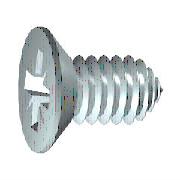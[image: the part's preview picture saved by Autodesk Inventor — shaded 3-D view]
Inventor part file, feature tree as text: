
AUTODESK INVENTOR PART (.ipt)
format: ipt  version: 2020 (Build 240168000, 168)  size: 263,680 bytes
history: native  units: mm (DEFAULTED — no unit token found)
features: extrude x2, plane x1, sketch x1
ambient origin geometry x8: Origin, YZ Plane, XZ Plane, XY Plane, X Axis, Y Axis, Z Axis, Center Point
bodies: Solid1 (feature_tree), Body (feature_tree)
feature tree (4):
  extrude  "Slot"  TaperAngle=45.0deg  [1 undecoded]
  extrude  "Star Cut"  Depth=2.2mm
  plane  "Work Plane2"
  sketch  "Sketch3"  dims[d0=32.0mm d2=45.0deg d3=4.2mm d5=8.4mm d6=4.4mm d7=4.625123mm d8=10.821041mm d9=2.51mm d16=90.0deg d10=45.0deg d11=1.76mm d12=4.4mm d13=0.515mm d14=4.4mm d15=45.0deg d17=0.515mm d18=2.6mm d19=-5.235988mm d20=29.4mm d21=0.0mm d22=2.1mm d23=3.7mm d25=0.0mm d26=2.2mm d66=25.4mm d27=0.872665mm d28=0.206mm d29=2.6mm d71=45.0deg d73=0.0mm d74=0.0mm]
note: 1 required parameter value undecoded (feature->parameter linkage not recoverable at this tier; creation-order binding heuristic only, values carry confidence <= 0.55)
